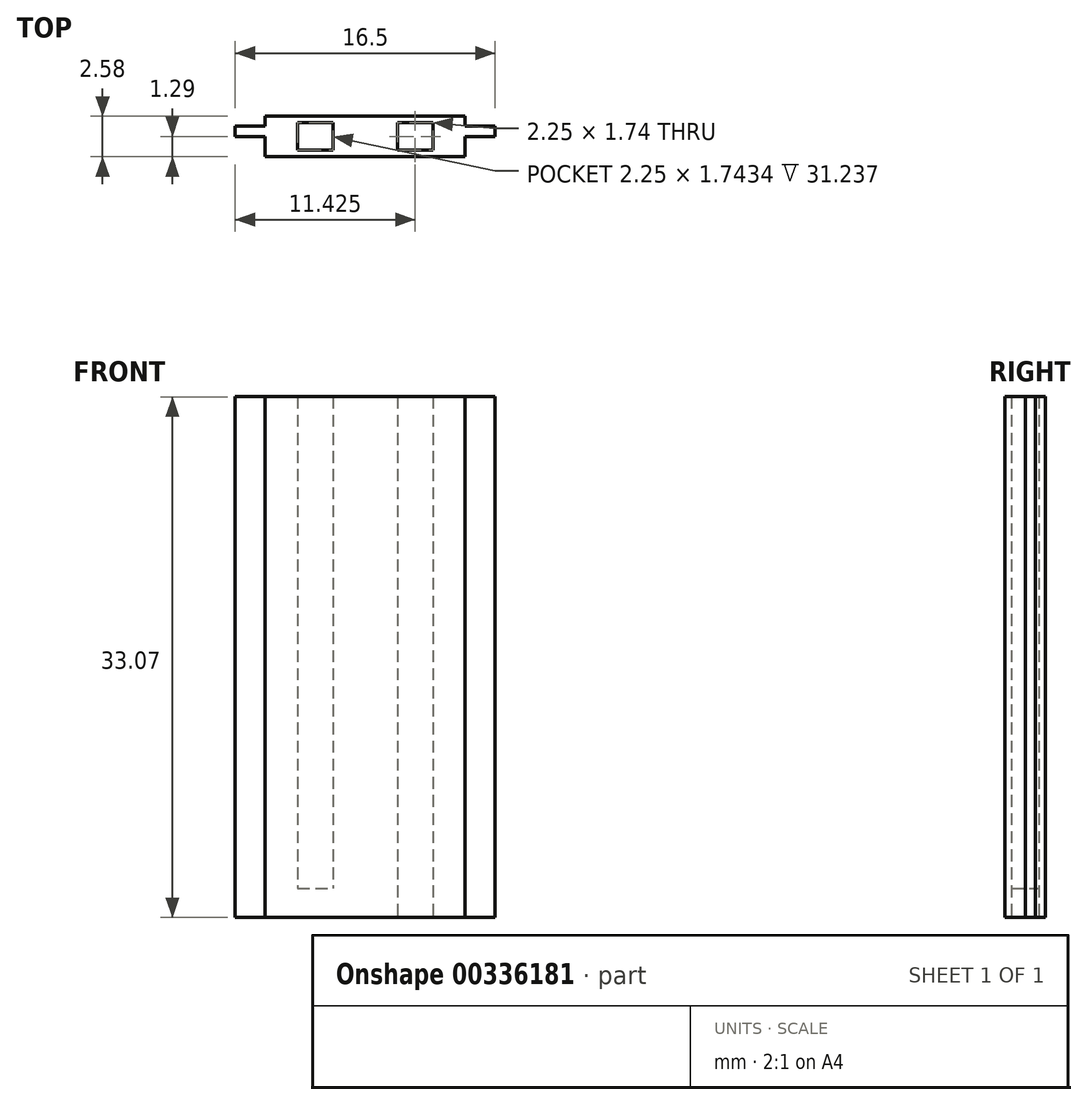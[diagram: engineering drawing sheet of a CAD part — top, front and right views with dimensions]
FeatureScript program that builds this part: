
annotation { "Feature Type Name" : "Feature", "Feature Type Description" : "" }
export const myFeature = defineFeature(function(context is Context, id is Id, definition is map)
    precondition{}
    {
        {
            var Q0;
            Q0=qCreatedBy(makeId("Top.planeOp"),FACE);
            var sketch = newSketch(context, id + "F0", { "sketchPlane" : qUnion([Q0])});
            skLineSegment(sketch, "E0.right", {"start": v(-6.35, 1.29) * mm, "end": v(-6.35, 0.64) * mm});
            skPoint(sketch, "E0.middle", {"position": v(0, 0) * mm});
            skPoint(sketch, "E1.middle", {"position": v(-3.18, 0) * mm});
            skPoint(sketch, "E2.start.orphan", {"position": v(-3.18, 0.64) * mm});
            skPoint(sketch, "E3.start.orphan", {"position": v(-3.18, -0.64) * mm});
            skLineSegment(sketch, "E4.MirrorCS", {"start": v(4.3, -0.87) * mm, "end": v(2.05, -0.87) * mm});
            skPoint(sketch, "E5.start.orphan", {"position": v(3.18, 0.64) * mm});
            skPoint(sketch, "E6.start.orphan", {"position": v(3.18, -0.64) * mm});
            skPoint(sketch, "E0.bottom.end.orphan", {"position": v(0, 1.29) * mm});
            skPoint(sketch, "E7.start.orphan", {"position": v(-6.35, 0) * mm});
            skPoint(sketch, "E0.top.end.orphan", {"position": v(0, -1.29) * mm});
            skPoint(sketch, "E1.right.end.orphan", {"position": v(-2.05, -0.87) * mm});
            skPoint(sketch, "E1.bottom.end.orphan", {"position": v(-2.05, 0.87) * mm});
            skPoint(sketch, "E1.left.end.orphan", {"position": v(-4.3, -0.87) * mm});
            skPoint(sketch, "E1.left.start.orphan", {"position": v(-4.3, 0.87) * mm});
            skLineSegment(sketch, "E8", {"start": v(6.35, 0.64) * mm, "end": v(8.25, 0.64) * mm});
            skLineSegment(sketch, "E9", {"start": v(8.25, 0.64) * mm, "end": v(8.25, 0) * mm});
            skLineSegment(sketch, "E10", {"start": v(-8.25, 0.64) * mm, "end": v(-6.35, 0.64) * mm});
            skLineSegment(sketch, "E11", {"start": v(-6.35, 0) * mm, "end": v(-8.25, 0) * mm});
            skLineSegment(sketch, "E12", {"start": v(-8.25, 0) * mm, "end": v(-8.25, 0.64) * mm});
            skLineSegment(sketch, "E13", {"start": v(6.35, 1.29) * mm, "end": v(6.35, 0.64) * mm});
            skLineSegment(sketch, "E14", {"start": v(8.25, 0) * mm, "end": v(6.35, 0) * mm});
            skLineSegment(sketch, "E15", {"start": v(-6.35, 1.29) * mm, "end": v(6.35, 1.29) * mm});
            skLineSegment(sketch, "E16", {"start": v(6.35, 0) * mm, "end": v(6.35, -1.29) * mm});
            skLineSegment(sketch, "E17", {"start": v(-6.35, -1.29) * mm, "end": v(-6.35, 0) * mm});
            skLineSegment(sketch, "E18", {"start": v(6.35, -1.29) * mm, "end": v(-6.35, -1.29) * mm});
            skLineSegment(sketch, "E19", {"start": v(-4.3, 0.87) * mm, "end": v(-2.05, 0.87) * mm});
            skLineSegment(sketch, "E20", {"start": v(-2.05, 0.87) * mm, "end": v(-2.05, -0.87) * mm});
            skLineSegment(sketch, "E21", {"start": v(-2.05, -0.87) * mm, "end": v(-4.3, -0.87) * mm});
            skLineSegment(sketch, "E22", {"start": v(-4.3, -0.87) * mm, "end": v(-4.3, 0.87) * mm});
            skLineSegment(sketch, "E23", {"start": v(4.3, 0.87) * mm, "end": v(4.3, -0.87) * mm});
            skLineSegment(sketch, "E24", {"start": v(2.05, 0.87) * mm, "end": v(2.05, 0.87) * mm});
            skLineSegment(sketch, "E25", {"start": v(4.3, 0.87) * mm, "end": v(2.05, 0.87) * mm});
            skLineSegment(sketch, "E26", {"start": v(2.05, 0.87) * mm, "end": v(2.05, -0.87) * mm});
            skSolve(sketch);
        }
        {
            var Q0;
            Q0=makeQuery(id+"F0.imprint","IMPRINT",FACE,{"disambiguationData":[TD([[makeQuery(id+"F0.imprint","IMPRINT",EDGE,{"derivedFrom":sQuery(id+"F0.wireOp",EDGE,"E0.right")}),1.0]])]});
            extrude(context, id + "F1", {"entities" : qUnion([Q0]), "depth" : 1.13 * mm});
        }
        {
            var Q0;
            Q0=sQuery(id+"F0.wireOp",EDGE,"E12");
            extrude(context, id + "F2", {"bodyType" : ToolBodyType.SURFACE, "surfaceEntities" : qUnion([Q0]), "depth" : 25.4 * mm});
        }
        {
            var Q0;
            Q0=makeQuery(id+"F0.imprint","IMPRINT",FACE,{"disambiguationData":[TD([[makeQuery(id+"F0.imprint","IMPRINT",EDGE,{"derivedFrom":sQuery(id+"F0.wireOp",EDGE,"E19")}),-1.0]])]});
            extrude(context, id + "F3", {"entities" : qUnion([Q0]), "operationType" : NewBodyOperationType.ADD, "depth" : 1.83 * mm});
        }
        {
            var Q0;
            Q0=makeQuery(id+"F0.imprint","IMPRINT",FACE,{"disambiguationData":[TD([[makeQuery(id+"F0.imprint","IMPRINT",EDGE,{"derivedFrom":sQuery(id+"F0.wireOp",EDGE,"E0.right")}),1.0]])]});
            extrude(context, id + "F4", {"entities" : qUnion([Q0]), "operationType" : NewBodyOperationType.ADD, "depth" : 33.07 * mm});
        }
    });
